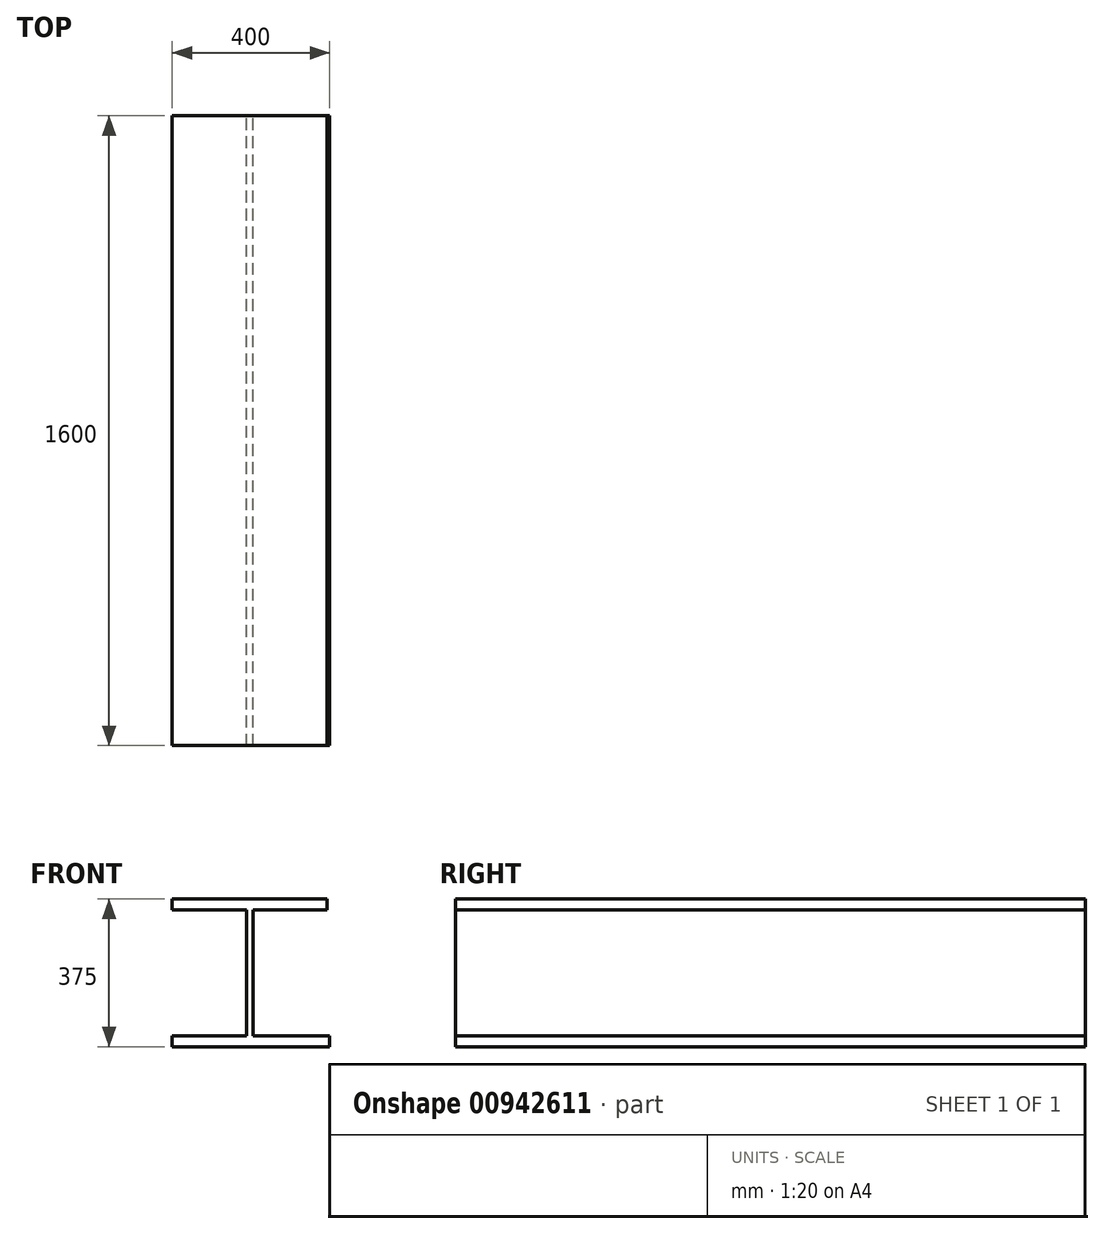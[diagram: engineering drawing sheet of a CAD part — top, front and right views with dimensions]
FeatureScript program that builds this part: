
annotation { "Feature Type Name" : "Feature", "Feature Type Description" : "" }
export const myFeature = defineFeature(function(context is Context, id is Id, definition is map)
    precondition{}
    {
        {
            var Q0;
            Q0=qCreatedBy(makeId("Front.planeOp"),FACE);
            var sketch = newSketch(context, id + "F0", { "sketchPlane" : qUnion([Q0])});
            skLineSegment(sketch, "E0.bottom", {"start": v(-208.82, 50.46) * mm, "end": v(185.18, 50.46) * mm});
            skLineSegment(sketch, "E0.top", {"start": v(-208.82, 22.76) * mm, "end": v(-20.47, 22.76) * mm});
            skLineSegment(sketch, "E0.left", {"start": v(-208.82, 50.46) * mm, "end": v(-208.82, 22.76) * mm});
            skLineSegment(sketch, "E0.right", {"start": v(185.18, 50.46) * mm, "end": v(185.18, 22.76) * mm});
            skLineSegment(sketch, "E1.bottom", {"start": v(-208.82, -296.84) * mm, "end": v(-20.47, -296.84) * mm});
            skLineSegment(sketch, "E1.top", {"start": v(-208.82, -324.54) * mm, "end": v(191.18, -324.54) * mm});
            skLineSegment(sketch, "E1.left", {"start": v(-208.82, -296.84) * mm, "end": v(-208.82, -324.54) * mm});
            skLineSegment(sketch, "E1.right", {"start": v(191.18, -296.84) * mm, "end": v(191.18, -324.54) * mm});
            skLineSegment(sketch, "E2", {"start": v(-11.82, 22.76) * mm, "end": v(-11.82, -296.84) * mm, "construction": true});
            skLineSegment(sketch, "E3", {"start": v(-20.47, 22.76) * mm, "end": v(-20.47, -296.84) * mm});
            skLineSegment(sketch, "E4", {"start": v(-3.17, 22.76) * mm, "end": v(-3.17, -296.84) * mm});
            skLineSegment(sketch, "E5.trimOffspring", {"start": v(-3.17, 22.76) * mm, "end": v(185.18, 22.76) * mm});
            skLineSegment(sketch, "E6.trimOffspring", {"start": v(-3.17, -296.84) * mm, "end": v(191.18, -296.84) * mm});
            skSolve(sketch);
        }
        {
            var Q0;
            Q0=makeQuery(id+"F0.imprint","IMPRINT",FACE,{"disambiguationData":[TD([[makeQuery(id+"F0.imprint","IMPRINT",EDGE,{"derivedFrom":sQuery(id+"F0.wireOp",EDGE,"E0.bottom")}),-1.0]])]});
            extrude(context, id + "F1", {"entities" : qUnion([Q0]), "depth" : 1600 * mm, "offsetDistance" : 25 * mm});
        }
    });
